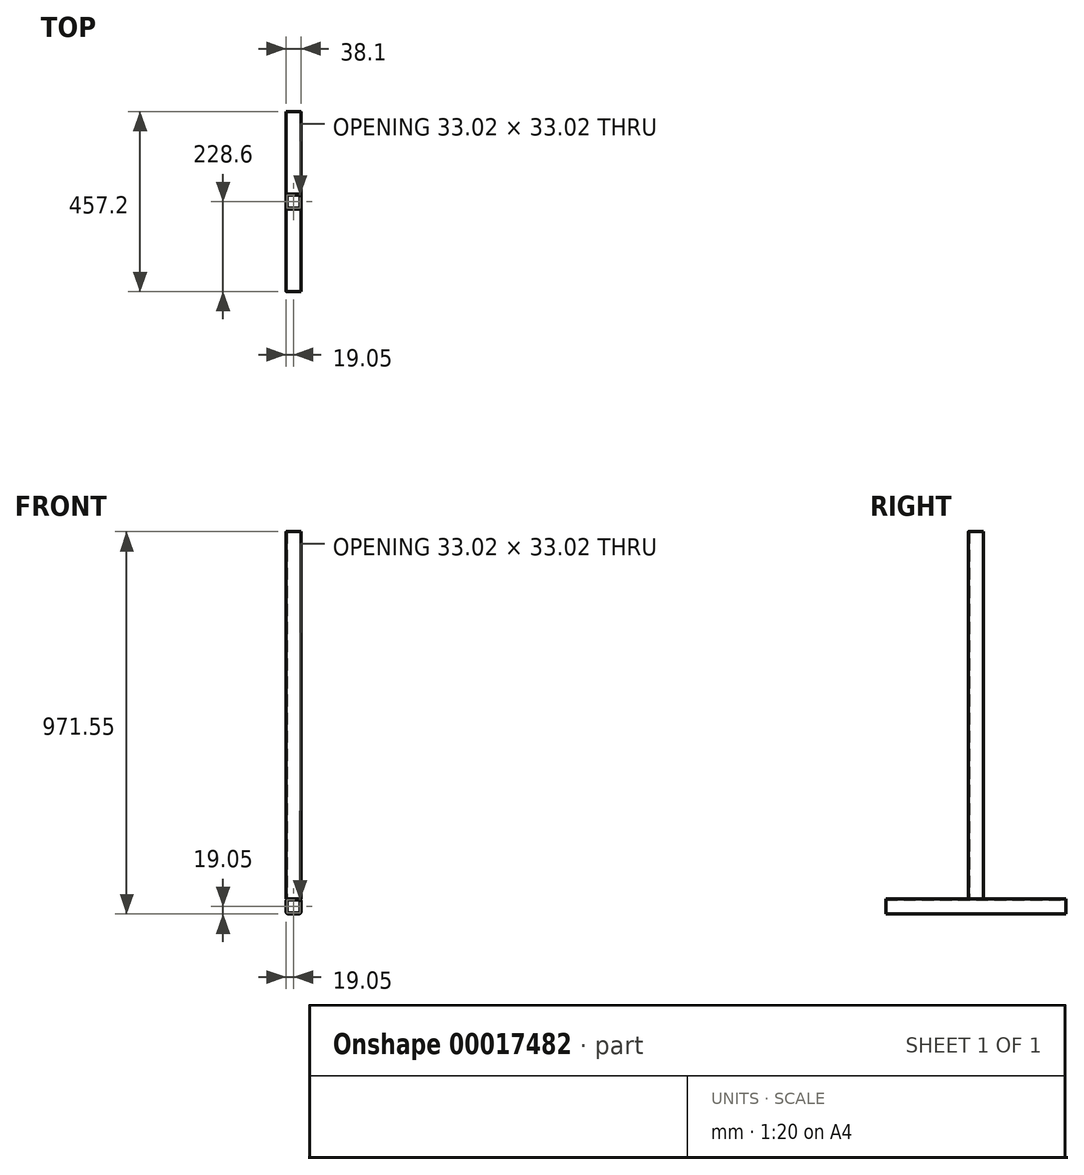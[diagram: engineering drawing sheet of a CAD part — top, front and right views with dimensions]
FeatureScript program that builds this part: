
annotation { "Feature Type Name" : "Feature", "Feature Type Description" : "" }
export const myFeature = defineFeature(function(context is Context, id is Id, definition is map)
    precondition{}
    {
        {
            var Q0;
            Q0=qCreatedBy(makeId("Top.planeOp"),FACE);
            var sketch = newSketch(context, id + "F0", { "sketchPlane" : qUnion([Q0])});
            skLineSegment(sketch, "E0.rect.bottom", {"start": v(12.7, 19.05) * mm, "end": v(-12.7, 19.05) * mm});
            skLineSegment(sketch, "E0.rect.top", {"start": v(12.7, -19.05) * mm, "end": v(-12.7, -19.05) * mm});
            skLineSegment(sketch, "E0.rect.left", {"start": v(19.05, 12.7) * mm, "end": v(19.05, -12.7) * mm});
            skLineSegment(sketch, "E0.rect.right", {"start": v(-19.05, 12.7) * mm, "end": v(-19.05, -12.7) * mm});
            skPoint(sketch, "E0.rect.middle", {"position": v(0, 0) * mm});
            skPoint(sketch, "E1.visualSharp", {"position": v(-19.05, 19.05) * mm});
            skArc(sketch, "E1.filletArc", {"start": v(-12.7, 19.05) * mm, "mid": v(-17.2, 17.2) * mm, "end": v(-19.05, 12.7) * mm});
            skPoint(sketch, "E2.visualSharp", {"position": v(19.05, 19.05) * mm});
            skArc(sketch, "E2.filletArc", {"start": v(19.05, 12.7) * mm, "mid": v(17.2, 17.2) * mm, "end": v(12.7, 19.05) * mm});
            skPoint(sketch, "E3.visualSharp", {"position": v(19.05, -19.05) * mm});
            skArc(sketch, "E3.filletArc", {"start": v(12.7, -19.05) * mm, "mid": v(17.2, -17.2) * mm, "end": v(19.05, -12.7) * mm});
            skPoint(sketch, "E4.visualSharp", {"position": v(-19.05, -19.05) * mm});
            skArc(sketch, "E4.filletArc", {"start": v(-19.05, -12.7) * mm, "mid": v(-17.2, -17.2) * mm, "end": v(-12.7, -19.05) * mm});
            skLineSegment(sketch, "E5.0", {"start": v(12.7, 16.51) * mm, "end": v(-12.7, 16.51) * mm});
            skArc(sketch, "E5.1", {"start": v(16.51, 12.7) * mm, "mid": v(15.4, 15.4) * mm, "end": v(12.7, 16.5) * mm});
            skLineSegment(sketch, "E5.2", {"start": v(16.51, 12.7) * mm, "end": v(16.51, -12.7) * mm});
            skArc(sketch, "E5.3", {"start": v(12.7, -16.5) * mm, "mid": v(15.4, -15.4) * mm, "end": v(16.51, -12.7) * mm});
            skLineSegment(sketch, "E5.4", {"start": v(12.7, -16.5) * mm, "end": v(-12.7, -16.5) * mm});
            skArc(sketch, "E5.5", {"start": v(-12.7, 16.51) * mm, "mid": v(-15.4, 15.4) * mm, "end": v(-16.51, 12.7) * mm});
            skArc(sketch, "E5.6", {"start": v(-16.51, -12.7) * mm, "mid": v(-15.4, -15.4) * mm, "end": v(-12.7, -16.5) * mm});
            skLineSegment(sketch, "E5.7", {"start": v(-16.51, 12.7) * mm, "end": v(-16.51, -12.7) * mm});
            skSolve(sketch);
        }
        {
            var Q0;
            Q0 = qSketchRegion(id + "F0", true);
            extrude(context, id + "F1", {"entities" : qUnion([Q0]), "depth" : 19.05 * mm, "hasSecondDirection" : true, "secondDirectionOppositeDirection" : true, "secondDirectionDepth" : 914.4 * mm});
        }
        {
            var Q0;
            Q0=qCreatedBy(makeId("Front.planeOp"),FACE);
            var sketch = newSketch(context, id + "F2", { "sketchPlane" : qUnion([Q0])});
            skLineSegment(sketch, "E6.bottom", {"start": v(12.7, -952.5) * mm, "end": v(-12.7, -952.5) * mm});
            skLineSegment(sketch, "E6.top", {"start": v(12.7, -914.4) * mm, "end": v(-12.7, -914.4) * mm});
            skLineSegment(sketch, "E6.left", {"start": v(19.05, -946.15) * mm, "end": v(19.05, -920.75) * mm});
            skLineSegment(sketch, "E6.right", {"start": v(-19.05, -946.15) * mm, "end": v(-19.05, -920.75) * mm});
            skPoint(sketch, "E7.visualSharp", {"position": v(19.05, -914.4) * mm});
            skArc(sketch, "E7.filletArc", {"start": v(19.05, -920.75) * mm, "mid": v(17.2, -916.26) * mm, "end": v(12.7, -914.4) * mm});
            skPoint(sketch, "E8.visualSharp", {"position": v(19.05, -952.5) * mm});
            skArc(sketch, "E8.filletArc", {"start": v(12.7, -952.5) * mm, "mid": v(17.2, -950.64) * mm, "end": v(19.05, -946.15) * mm});
            skPoint(sketch, "E9.visualSharp", {"position": v(-19.05, -952.5) * mm});
            skArc(sketch, "E9.filletArc", {"start": v(-19.05, -946.15) * mm, "mid": v(-17.2, -950.64) * mm, "end": v(-12.7, -952.5) * mm});
            skPoint(sketch, "E10.visualSharp", {"position": v(-19.05, -914.4) * mm});
            skArc(sketch, "E10.filletArc", {"start": v(-12.7, -914.4) * mm, "mid": v(-17.2, -916.26) * mm, "end": v(-19.05, -920.75) * mm});
            skArc(sketch, "E11.0", {"start": v(16.51, -920.75) * mm, "mid": v(15.4, -918.06) * mm, "end": v(12.7, -916.94) * mm});
            skLineSegment(sketch, "E11.1", {"start": v(16.51, -946.15) * mm, "end": v(16.51, -920.75) * mm});
            skArc(sketch, "E11.2", {"start": v(12.7, -949.96) * mm, "mid": v(15.4, -948.84) * mm, "end": v(16.51, -946.15) * mm});
            skLineSegment(sketch, "E11.3", {"start": v(12.7, -949.96) * mm, "end": v(-12.7, -949.96) * mm});
            skArc(sketch, "E11.4", {"start": v(-16.51, -946.15) * mm, "mid": v(-15.4, -948.84) * mm, "end": v(-12.7, -949.96) * mm});
            skLineSegment(sketch, "E11.5", {"start": v(12.7, -916.94) * mm, "end": v(-12.7, -916.94) * mm});
            skLineSegment(sketch, "E11.6", {"start": v(-16.51, -946.15) * mm, "end": v(-16.51, -920.75) * mm});
            skArc(sketch, "E11.7", {"start": v(-12.7, -916.94) * mm, "mid": v(-15.4, -918.06) * mm, "end": v(-16.51, -920.75) * mm});
            skLineSegment(sketch, "E12.2", {"start": v(6.35, 12.7) * mm, "end": v(-6.35, 12.7) * mm});
            skSolve(sketch);
        }
        {
            var Q0;
            Q0 = qSketchRegion(id + "F2", true);
            extrude(context, id + "F3", {"entities" : qUnion([Q0]), "endBound" : BoundingType.SYMMETRIC, "depth" : 457.2 * mm});
        }
    });
